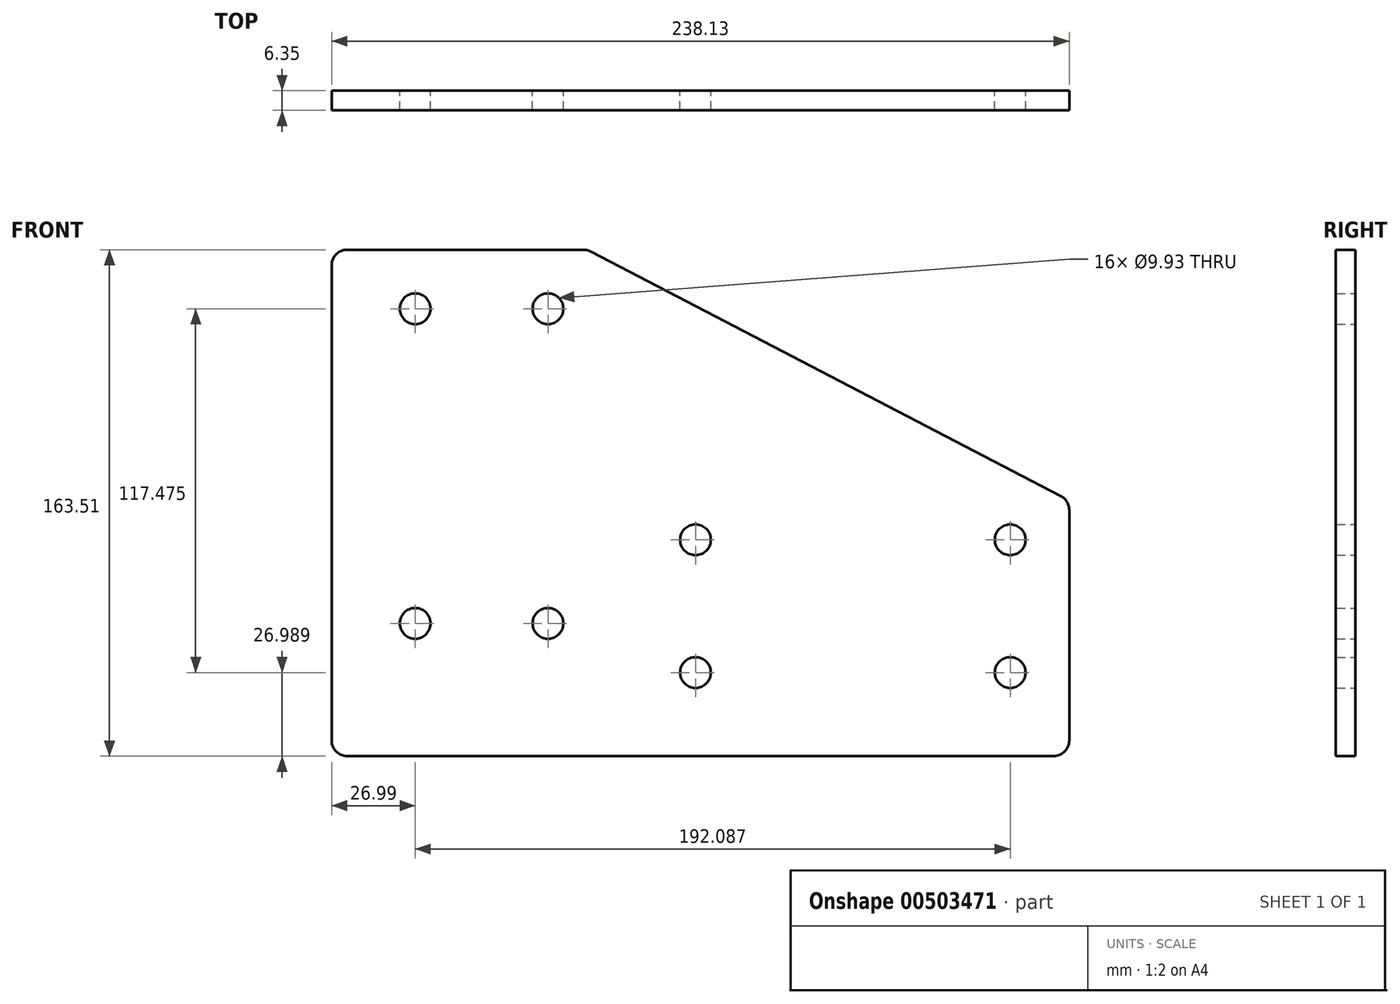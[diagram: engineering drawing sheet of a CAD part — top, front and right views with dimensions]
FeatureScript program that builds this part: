
annotation { "Feature Type Name" : "Feature", "Feature Type Description" : "" }
export const myFeature = defineFeature(function(context is Context, id is Id, definition is map)
    precondition{}
    {
        {
            var Q0;
            Q0=qCreatedBy(makeId("Front.planeOp"),FACE);
            var sketch = newSketch(context, id + "F0", { "sketchPlane" : qUnion([Q0])});
            skLineSegment(sketch, "E0.top", {"start": v(141.38, 0.21) * mm, "end": v(141.38, 82.76) * mm});
            skLineSegment(sketch, "E0.left", {"start": v(-96.75, 0.21) * mm, "end": v(141.38, 0.21) * mm});
            skCircle(sketch, "E1", {"center": v(-69.76, 43.07) * mm, "radius": 4.97 * mm});
            skCircle(sketch, "E2", {"center": v(-26.9, 43.07) * mm, "radius": 4.97 * mm});
            skLineSegment(sketch, "E3", {"start": v(20.73, 70.06) * mm, "end": v(20.73, 0.21) * mm, "construction": true});
            skCircle(sketch, "E4", {"center": v(20.73, 70.06) * mm, "radius": 4.97 * mm});
            skCircle(sketch, "E5", {"center": v(20.73, 27.2) * mm, "radius": 4.97 * mm});
            skLineSegment(sketch, "E6", {"start": v(-96.75, 163.72) * mm, "end": v(-14.2, 163.72) * mm});
            skCircle(sketch, "E7", {"center": v(-69.76, 144.67) * mm, "radius": 4.97 * mm});
            skCircle(sketch, "E8", {"center": v(-26.9, 144.67) * mm, "radius": 4.97 * mm});
            skLineSegment(sketch, "E9", {"start": v(54.79, -23.6) * mm, "end": v(-125.88, -23.6) * mm});
            skLineSegment(sketch, "E10", {"start": v(-69.76, 144.67) * mm, "end": v(-120.56, 144.67) * mm});
            skLineSegment(sketch, "E11", {"start": v(-96.75, 163.72) * mm, "end": v(-96.75, 0.21) * mm});
            skCircle(sketch, "E12", {"center": v(122.33, 70.06) * mm, "radius": 4.97 * mm});
            skCircle(sketch, "E13", {"center": v(122.33, 27.2) * mm, "radius": 4.97 * mm});
            skLineSegment(sketch, "E14", {"start": v(-14.2, 163.72) * mm, "end": v(141.38, 82.76) * mm});
            skSolve(sketch);
        }
        {
            var Q0;
            Q0 = qSketchRegion(id + "F0", true);
            extrude(context, id + "F1", {"entities" : qUnion([Q0]), "depth" : 6.35 * mm, "offsetDistance" : 25.4 * mm});
        }
        {
            var Q0;
            Q0=makeQuery(id+"F1.opExtrude","SWEPT_EDGE",EDGE,{"disambiguationData":[OSD([sQuery(id+"FNj83cxcOXgbGo6_0.wireOp",EDGE,"YLJfwgbZ-YHyl-cvS9-Tr0C-U3R6be7mc2fx.top"),sQuery(id+"FNj83cxcOXgbGo6_0.wireOp",EDGE,"YLJfwgbZ-YHyl-cvS9-Tr0C-U3R6be7mc2fx.left")])]});
            var Q1;
            Q1=makeQuery(id+"F1.opExtrude","SWEPT_EDGE",EDGE,{"disambiguationData":[OSD([sQuery(id+"FNj83cxcOXgbGo6_0.wireOp",EDGE,"YLJfwgbZ-YHyl-cvS9-Tr0C-U3R6be7mc2fx.bottom"),sQuery(id+"FNj83cxcOXgbGo6_0.wireOp",EDGE,"YLJfwgbZ-YHyl-cvS9-Tr0C-U3R6be7mc2fx.left")])]});
            var Q2;
            Q2=makeQuery(id+"F1.opExtrude","SWEPT_EDGE",EDGE,{"disambiguationData":[OSD([sQuery(id+"FNj83cxcOXgbGo6_0.wireOp",EDGE,"YLJfwgbZ-YHyl-cvS9-Tr0C-U3R6be7mc2fx.bottom"),sQuery(id+"FNj83cxcOXgbGo6_0.wireOp",EDGE,"YLJfwgbZ-YHyl-cvS9-Tr0C-U3R6be7mc2fx.right")])]});
            var Q3;
            Q3=makeQuery(id+"F1.opExtrude","SWEPT_EDGE",EDGE,{"disambiguationData":[OSD([sQuery(id+"FNj83cxcOXgbGo6_0.wireOp",EDGE,"YLJfwgbZ-YHyl-cvS9-Tr0C-U3R6be7mc2fx.top"),sQuery(id+"FNj83cxcOXgbGo6_0.wireOp",EDGE,"YLJfwgbZ-YHyl-cvS9-Tr0C-U3R6be7mc2fx.right")])]});
            var Q4;
            Q4=makeQuery(id+"F1.opExtrude","SWEPT_EDGE",EDGE,{"disambiguationData":[OSD([sQuery(id+"FNj83cxcOXgbGo6_0.wireOp",EDGE,"av35LSo8-nv1P-ecUa-bM0M-DhvCoOtsW4H1"),sQuery(id+"FNj83cxcOXgbGo6_0.wireOp",EDGE,"TwLJLxqH-c4EN-Iaun-qm5o-bjvqboWOfFqz")])]});
            var Q5;
            Q5=makeQuery(id+"F1.opExtrude","SWEPT_EDGE",EDGE,{"disambiguationData":[OSD([sQuery(id+"FNj83cxcOXgbGo6_0.wireOp",EDGE,"TwLJLxqH-c4EN-Iaun-qm5o-bjvqboWOfFqz"),sQuery(id+"FNj83cxcOXgbGo6_0.wireOp",EDGE,"qYVnyuXa-Kr3J-J92z-Ydc9-I5E6tiZ9RHag")])]});
            var Q6;
            Q6=makeQuery(id+"F1.opExtrude","SWEPT_EDGE",EDGE,{"disambiguationData":[OSD([sQuery(id+"F0.wireOp",EDGE,"E0.left"),sQuery(id+"F0.wireOp",EDGE,"E11")])]});
            var Q7;
            Q7=makeQuery(id+"F1.opExtrude","SWEPT_EDGE",EDGE,{"disambiguationData":[OSD([sQuery(id+"F0.wireOp",EDGE,"E6"),sQuery(id+"F0.wireOp",EDGE,"E11")])]});
            var Q8;
            Q8=makeQuery(id+"F1.opExtrude","SWEPT_EDGE",EDGE,{"disambiguationData":[OSD([sQuery(id+"F0.wireOp",EDGE,"E6"),sQuery(id+"F0.wireOp",EDGE,"E14")])]});
            var Q9;
            Q9=makeQuery(id+"F1.opExtrude","SWEPT_EDGE",EDGE,{"disambiguationData":[OSD([sQuery(id+"F0.wireOp",EDGE,"E0.top"),sQuery(id+"F0.wireOp",EDGE,"E14")])]});
            var Q10;
            Q10=makeQuery(id+"F1.opExtrude","SWEPT_EDGE",EDGE,{"disambiguationData":[OSD([sQuery(id+"F0.wireOp",EDGE,"E0.top"),sQuery(id+"F0.wireOp",EDGE,"E0.left")])]});
            fillet(context, id + "F2", {"entities" : qUnion([Q0, Q1, Q2, Q3, Q4, Q5, Q6, Q7, Q8, Q9, Q10]), "radius" : 5.08 * mm, "tangentPropagation" : true, "allowEdgeOverflow" : false});
        }
    });
